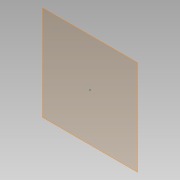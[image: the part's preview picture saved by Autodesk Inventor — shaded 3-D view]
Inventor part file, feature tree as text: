
AUTODESK INVENTOR PART (.ipt)
format: ipt  version: 2013 (Build 170138000, 138)  size: 91,136 bytes
history: native  units: in
note: dims shown in document units (in); Inventor stores cm internally (conversion verified against a paired STEP export)
features: other x78, reference x8, plane x1, sketch x1, pattern_linear x1
ambient origin geometry x8: Origin, YZ Plane, XZ Plane, XY Plane, X Axis, Y Axis, Z Axis, Center Point
feature tree (89):
  plane  "Work Plane1"
  sketch  "Sketch1"  dims[d0=30.7382in]
  other  "Work Point1"
  pattern_linear  "Rectangular Pattern1"  [2 undecoded]
  reference  "Reference1"
  reference  "Reference2"
  reference  "Reference3"
  reference  "Reference4"
  reference  "Reference5"
  reference  "Reference6"
  reference  "Reference7"
  reference  "Reference8"
  other  "Work Point2"
  other  "Work Point3"
  other  "Work Point4"
  other  "Work Point5"
  other  "Work Point6"
  other  "Work Point7"
  other  "Work Point8"
  other  "Work Point9"
  other  "Work Point10"
  other  "Work Point11"
  other  "Work Point12"
  other  "Work Point13"
  other  "Work Point14"
  other  "Work Point15"
  other  "Work Point16"
  other  "Work Point17"
  other  "Work Point18"
  other  "Work Point19"
  other  "Work Point20"
  other  "Work Point21"
  other  "Work Point22"
  other  "Work Point23"
  other  "Work Point24"
  other  "Work Point25"
  other  "Work Point26"
  other  "Work Point27"
  other  "Work Point28"
  other  "Work Point29"
  other  "Work Point30"
  other  "Work Point31"
  other  "Work Point32"
  other  "Work Point33"
  other  "Work Point34"
  other  "Work Point35"
  other  "Work Point36"
  other  "Work Point37"
  other  "Work Point38"
  other  "Work Point39"
  other  "Work Point40"
  other  "Work Point41"
  other  "Work Point42"
  other  "Work Point43"
  other  "Work Point44"
  other  "Work Point45"
  other  "Work Point46"
  other  "Work Point47"
  other  "Work Point48"
  other  "Work Point49"
  other  "Work Point50"
  other  "Work Point51"
  other  "Work Point52"
  other  "Work Point53"
  other  "Work Point54"
  other  "Work Point55"
  other  "Work Point56"
  other  "Work Point57"
  other  "Work Point58"
  other  "Work Point59"
  other  "Work Point60"
  other  "Work Point61"
  other  "Work Point62"
  other  "Work Point63"
  other  "Work Point64"
  other  "Work Point65"
  other  "Work Point66"
  other  "Work Point67"
  other  "Work Point68"
  other  "Work Point69"
  other  "Work Point70"
  other  "Work Point71"
  other  "Work Point72"
  other  "Work Point73"
  other  "Work Point74"
  other  "Work Point75"
  other  "Work Point76"
  other  "Work Point77"
  other  "Work Point78"
note: 2 required parameter values undecoded (feature->parameter linkage not recoverable at this tier; creation-order binding heuristic only, values carry confidence <= 0.55)
